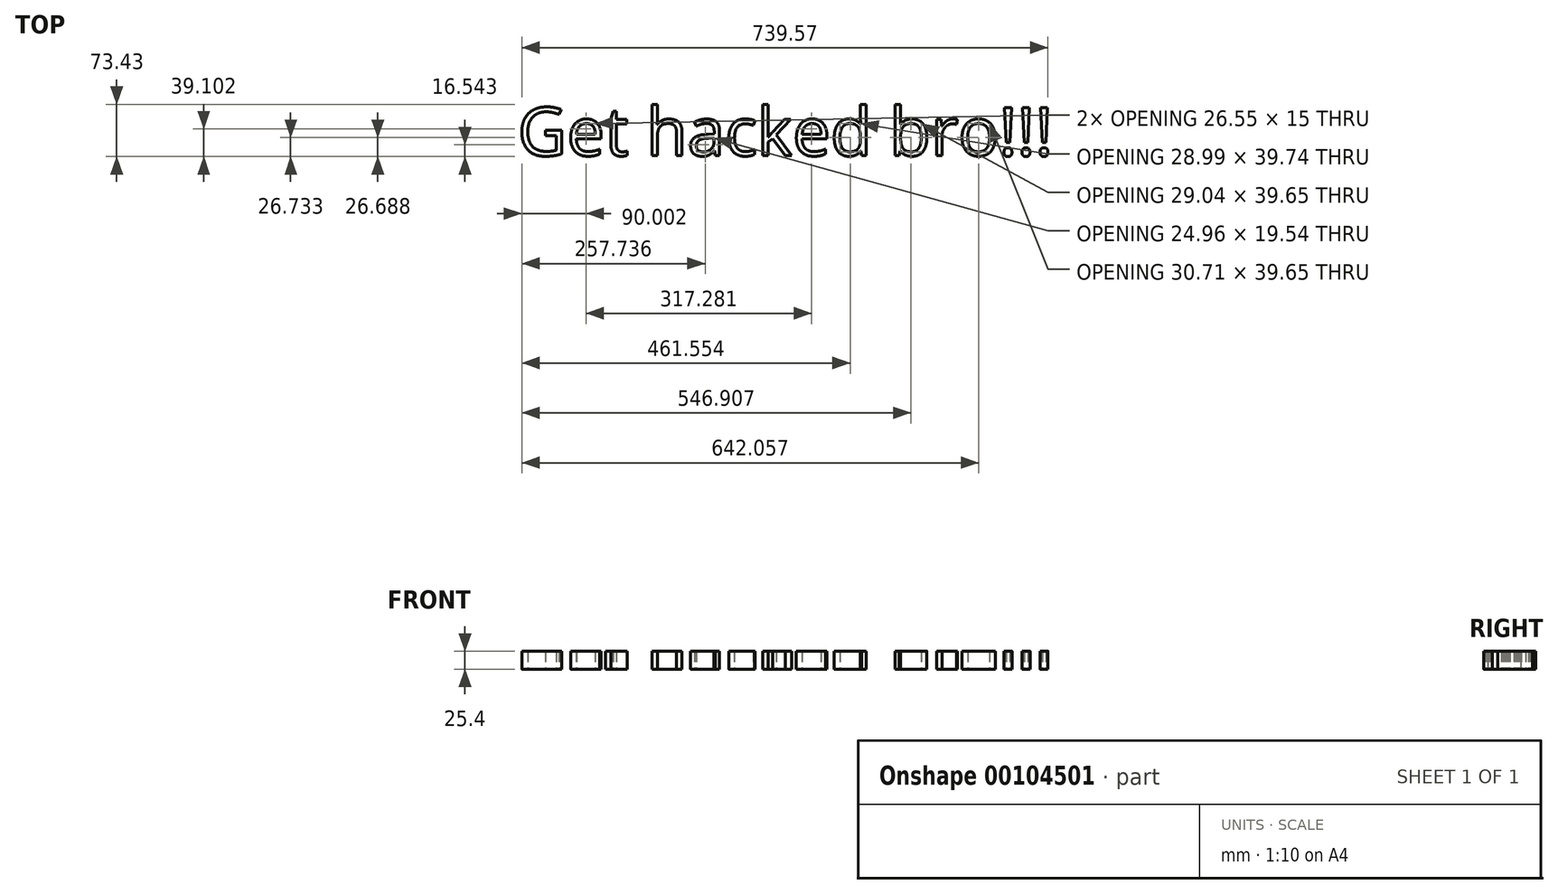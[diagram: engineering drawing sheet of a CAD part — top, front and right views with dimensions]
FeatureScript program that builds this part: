
annotation { "Feature Type Name" : "Feature", "Feature Type Description" : "" }
export const myFeature = defineFeature(function(context is Context, id is Id, definition is map)
    precondition{}
    {
        {
            var Q0;
            Q0=qCreatedBy(makeId("Top.planeOp"),FACE);
            var sketch = newSketch(context, id + "F0", { "sketchPlane" : qUnion([Q0])});
            skText(sketch, "E0", { "text": "Get hacked bro!!!", "fontName": "OpenSans-Regular.ttf"});
            const initialGuessF0  = {"E0": [-0.11669, -0.03123, 1, 0, 0.0683]};
            skSetInitialGuess(sketch, initialGuessF0);
            skSolve(sketch);
        }
        {
            var Q0;
            Q0 = qSketchRegion(id + "F0", true);
            extrude(context, id + "F1", {"entities" : qUnion([Q0]), "depth" : 25.4 * mm});
        }
    });
